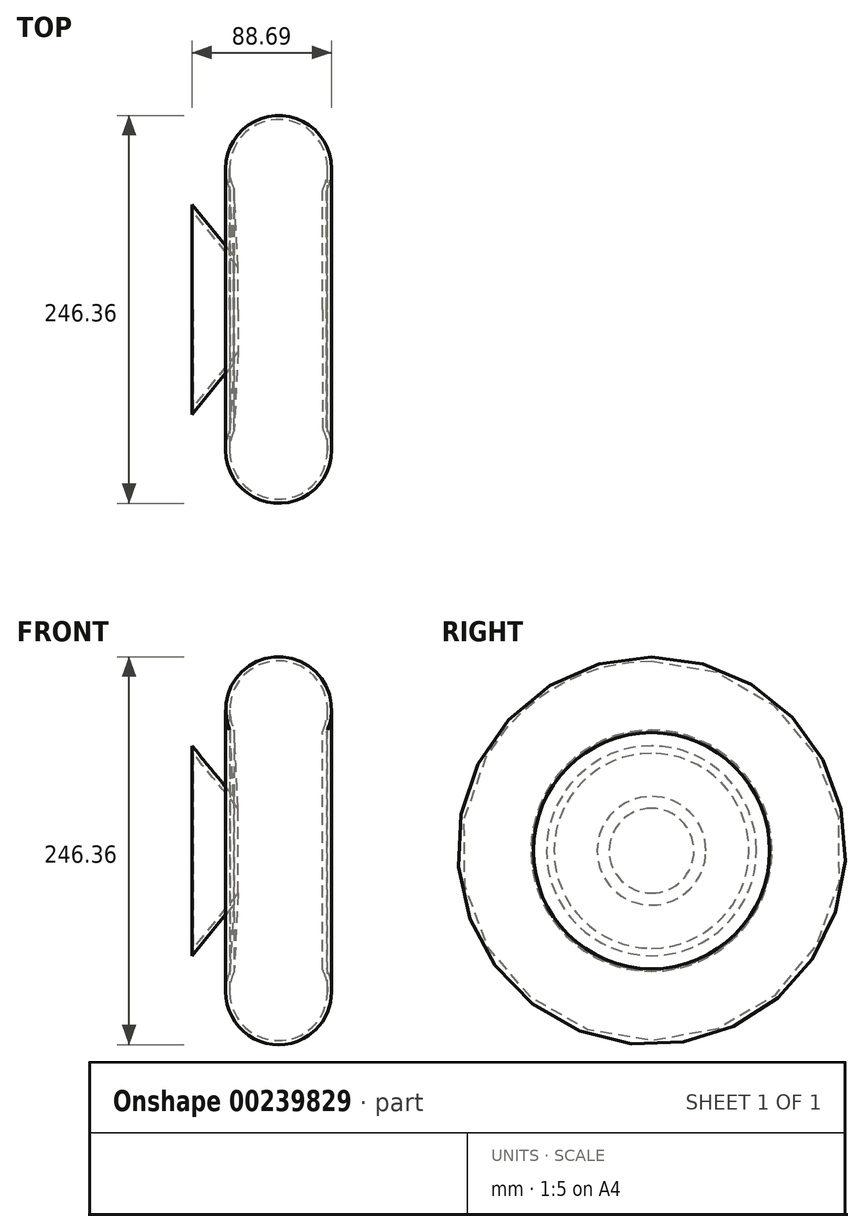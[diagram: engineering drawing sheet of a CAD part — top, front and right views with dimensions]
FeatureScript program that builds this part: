
annotation { "Feature Type Name" : "Feature", "Feature Type Description" : "" }
export const myFeature = defineFeature(function(context is Context, id is Id, definition is map)
    precondition{}
    {
        {
            var Q0;
            Q0=qCreatedBy(makeId("Front.planeOp"),FACE);
            var sketch = newSketch(context, id + "F0", { "sketchPlane" : qUnion([Q0])});
            skLineSegment(sketch, "E0", {"start": v(-1.6, 0) * mm, "end": v(-76.75, 0) * mm});
            skLineSegment(sketch, "E1", {"start": v(-76.75, 0) * mm, "end": v(0, 0) * mm});
            skLineSegment(sketch, "E2", {"start": v(0, 0) * mm, "end": v(0, 75) * mm});
            skLineSegment(sketch, "E3", {"start": v(-76.75, 0) * mm, "end": v(-85.37, 66.65) * mm});
            skLineSegment(sketch, "E4", {"start": v(-85.37, 66.65) * mm, "end": v(-59.05, 34.5) * mm});
            skLineSegment(sketch, "E5", {"start": v(-59.05, 34.5) * mm, "end": v(-61.07, 76) * mm});
            skArc(sketch, "E6", {"start": v(0, 75) * mm, "mid": v(-29.75, 123.18) * mm, "end": v(-61.07, 76) * mm});
            skSolve(sketch);
        }
        {
            var Q0;
            {var subQ1=sQuery(id+"F0.wireOp",EDGE,"E2");Q0=makeQuery(id+"F0.imprint","IMPRINT",FACE,{"disambiguationData":[TD([[makeQuery(id+"F0.imprint","IMPRINT",EDGE,{"derivedFrom":subQ1}),1.0]])]});}
            var Q1;
            Q1=sQuery(id+"F0.wireOp",EDGE,"E1");
            revolve(context, id + "F1", {"entities" : qUnion([Q0]), "axis" : qUnion([Q1]), "revolveType" : RevolveType.FULL});
        }
        {
            var Q0;
            Q0=makeQuery(id+"F1.opRevolve","SWEPT_FACE",FACE,{"disambiguationData":[OSD([sQuery(id+"F0.wireOp",EDGE,"E3")])]});
            shell(context, id + "F2", {"entities" : qUnion([Q0]), "thickness" : 2.54 * mm});
        }
    });
